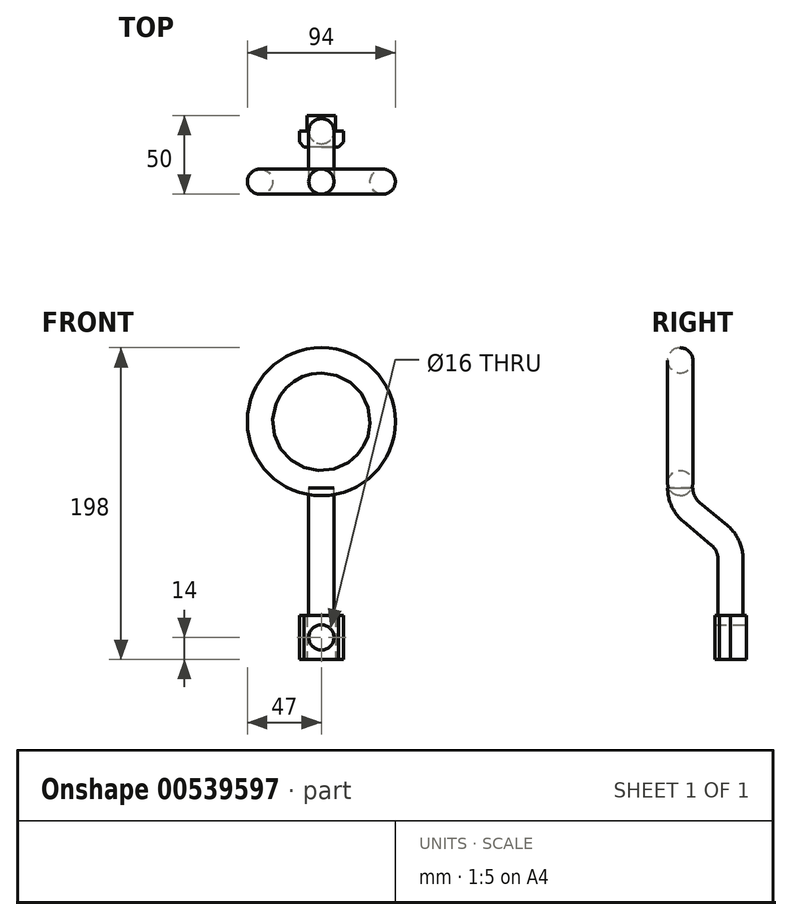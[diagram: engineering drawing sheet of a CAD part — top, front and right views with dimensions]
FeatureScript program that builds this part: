
annotation { "Feature Type Name" : "Feature", "Feature Type Description" : "" }
export const myFeature = defineFeature(function(context is Context, id is Id, definition is map)
    precondition{}
    {
        {
            var Q0;
            Q0=qCreatedBy(makeId("Top.planeOp"),FACE);
            var sketch = newSketch(context, id + "F0", { "sketchPlane" : qUnion([Q0])});
            skCircle(sketch, "E0", {"center": v(0, 0) * mm, "radius": 8 * mm});
            skSolve(sketch);
        }
        {
            var Q0;
            Q0=qCreatedBy(makeId("Top.planeOp"),FACE);
            var sketch = newSketch(context, id + "F1", { "sketchPlane" : qUnion([Q0])});
            skCircle(sketch, "E1", {"center": v(-39, 0) * mm, "radius": 8 * mm});
            skSolve(sketch);
        }
        {
            var Q0;
            Q0=qCreatedBy(makeId("Right.planeOp"),FACE);
            var sketch = newSketch(context, id + "F2", { "sketchPlane" : qUnion([Q0])});
            skLineSegment(sketch, "E2", {"start": v(45, 0) * mm, "end": v(-105, 0) * mm});
            skSolve(sketch);
        }
        {
            var Q0;
            Q0 = qSketchRegion(id + "F1", true);
            var Q1;
            Q1=sQuery(id+"F2.wireOp",EDGE,"E2");
            revolve(context, id + "F3", {"entities" : qUnion([Q0]), "axis" : qUnion([Q1]), "revolveType" : RevolveType.FULL});
        }
        {
            var Q0;
            Q0=qCreatedBy(makeId("Top.planeOp"),FACE);
            cPlane(context, id + "F4", {"entities" : qUnion([Q0]), "cplaneType" : CPlaneType.OFFSET, "offset" : 39 * mm, "width" : 150 * mm, "height" : 150 * mm});
        }
        {
            var Q0;
            Q0=qCreatedBy(id+"F4.planeOp",FACE);
            cPlane(context, id + "F5", {"entities" : qUnion([Q0]), "cplaneType" : CPlaneType.OFFSET, "offset" : 190 * mm, "oppositeDirection" : true, "width" : 150 * mm, "height" : 150 * mm});
        }
        {
            var Q0;
            Q0=qCreatedBy(id+"F5.planeOp",FACE);
            var sketch = newSketch(context, id + "F6", { "sketchPlane" : qUnion([Q0])});
            skLineSegment(sketch, "E3", {"start": v(0, 22) * mm, "end": v(-11, 22) * mm});
            skLineSegment(sketch, "E4", {"start": v(-11, 22) * mm, "end": v(-14, 25) * mm});
            skLineSegment(sketch, "E5", {"start": v(-14, 25) * mm, "end": v(-14, 32) * mm});
            skLineSegment(sketch, "E6", {"start": v(-14, 32) * mm, "end": v(-9, 32) * mm});
            skLineSegment(sketch, "E7", {"start": v(-9, 32) * mm, "end": v(-9, 42) * mm});
            skLineSegment(sketch, "E8", {"start": v(-9, 42) * mm, "end": v(0, 42) * mm});
            skLineSegment(sketch, "E9.MirrorCS", {"start": v(14, 32) * mm, "end": v(9, 32) * mm});
            skLineSegment(sketch, "E10.MirrorCS", {"start": v(14, 25) * mm, "end": v(14, 32) * mm});
            skLineSegment(sketch, "E11.MirrorCS", {"start": v(9, 32) * mm, "end": v(9, 42) * mm});
            skLineSegment(sketch, "E12.MirrorCS", {"start": v(11, 22) * mm, "end": v(14, 25) * mm});
            skLineSegment(sketch, "E13.MirrorCS", {"start": v(9, 42) * mm, "end": v(0, 42) * mm});
            skLineSegment(sketch, "E14.MirrorCS", {"start": v(0, 22) * mm, "end": v(11, 22) * mm});
            skSolve(sketch);
        }
        {
            var Q0;
            Q0 = qSketchRegion(id + "F6", true);
            extrude(context, id + "F7", {"entities" : qUnion([Q0]), "depth" : 28 * mm, "offsetDistance" : 25 * mm});
        }
        {
            var Q0;
            Q0=makeQuery(id+"F7.opExtrude","SWEPT_FACE",FACE,{"disambiguationData":[OSD([sQuery(id+"F6.wireOp",EDGE,"E8"),sQuery(id+"F6.wireOp",EDGE,"E13.MirrorCS")])]});
            var sketch = newSketch(context, id + "F8", { "sketchPlane" : qUnion([Q0])});
            skCircle(sketch, "E15", {"center": v(0, -137) * mm, "radius": 8 * mm});
            skPoint(sketch, "E15.centerSnap0", {"position": v(0, -151) * mm});
            skSolve(sketch);
        }
        {
            var Q0;
            Q0 = qSketchRegion(id + "F8", true);
            extrude(context, id + "F9", {"entities" : qUnion([Q0]), "operationType" : NewBodyOperationType.REMOVE, "oppositeDirection" : true, "depth" : 25 * mm, "offsetDistance" : 25 * mm});
        }
        {
            var Q0;
            Q0=qCreatedBy(makeId("Right.planeOp"),FACE);
            var sketch = newSketch(context, id + "F10", { "sketchPlane" : qUnion([Q0])});
            skLineSegment(sketch, "E16", {"start": v(7.2, -57.34) * mm, "end": v(24.8, -72) * mm});
            skLineSegment(sketch, "E17", {"start": v(32, -87.37) * mm, "end": v(32, -123) * mm});
            skLineSegment(sketch, "E18", {"start": v(0, -41.97) * mm, "end": v(0, -30) * mm});
            skPoint(sketch, "E19.visualSharp", {"position": v(0, -51.34) * mm});
            skArc(sketch, "E19.filletArc", {"start": v(0, -41.97) * mm, "mid": v(1.89, -50.46) * mm, "end": v(7.2, -57.34) * mm});
            skPoint(sketch, "E20.visualSharp", {"position": v(32, -78) * mm});
            skArc(sketch, "E20.filletArc", {"start": v(32, -87.37) * mm, "mid": v(30.11, -78.88) * mm, "end": v(24.8, -72) * mm});
            skSolve(sketch);
        }
        {
            var Q0;
            Q0=makeQuery(id+"F7.opExtrude","CAP_FACE",FACE,{"disambiguationData":[OSD([sQuery(id+"F6.wireOp",EDGE,"E3"),sQuery(id+"F6.wireOp",EDGE,"E4"),sQuery(id+"F6.wireOp",EDGE,"E5"),sQuery(id+"F6.wireOp",EDGE,"E6"),sQuery(id+"F6.wireOp",EDGE,"E7"),sQuery(id+"F6.wireOp",EDGE,"E8"),sQuery(id+"F6.wireOp",EDGE,"E9.MirrorCS"),sQuery(id+"F6.wireOp",EDGE,"E10.MirrorCS"),sQuery(id+"F6.wireOp",EDGE,"E11.MirrorCS"),sQuery(id+"F6.wireOp",EDGE,"E12.MirrorCS"),sQuery(id+"F6.wireOp",EDGE,"E13.MirrorCS"),sQuery(id+"F6.wireOp",EDGE,"E14.MirrorCS")])],"isStart":false});
            var sketch = newSketch(context, id + "F11", { "sketchPlane" : qUnion([Q0])});
            skCircle(sketch, "E21", {"center": v(0, 32) * mm, "radius": 8 * mm});
            skSolve(sketch);
        }
        {
            var Q0;
            Q0=makeQuery(id+"F11.imprint","IMPRINT",FACE,{"disambiguationData":[TD([[makeQuery(id+"F11.imprint","IMPRINT",EDGE,{"derivedFrom":sQuery(id+"F11.wireOp",EDGE,"E21")}),1.0]])]});
            var Q1;
            Q1=sQuery(id+"F10.wireOp",EDGE,"E17");
            var Q2;
            Q2=sQuery(id+"F10.wireOp",EDGE,"E20.filletArc");
            var Q3;
            Q3=sQuery(id+"F10.wireOp",EDGE,"E16");
            var Q4;
            Q4=sQuery(id+"F10.wireOp",EDGE,"E19.filletArc");
            sweep(context, id + "F12", {"profiles" : qUnion([Q0]), "path" : qUnion([Q1, Q2, Q3, Q4])});
        }
    });
